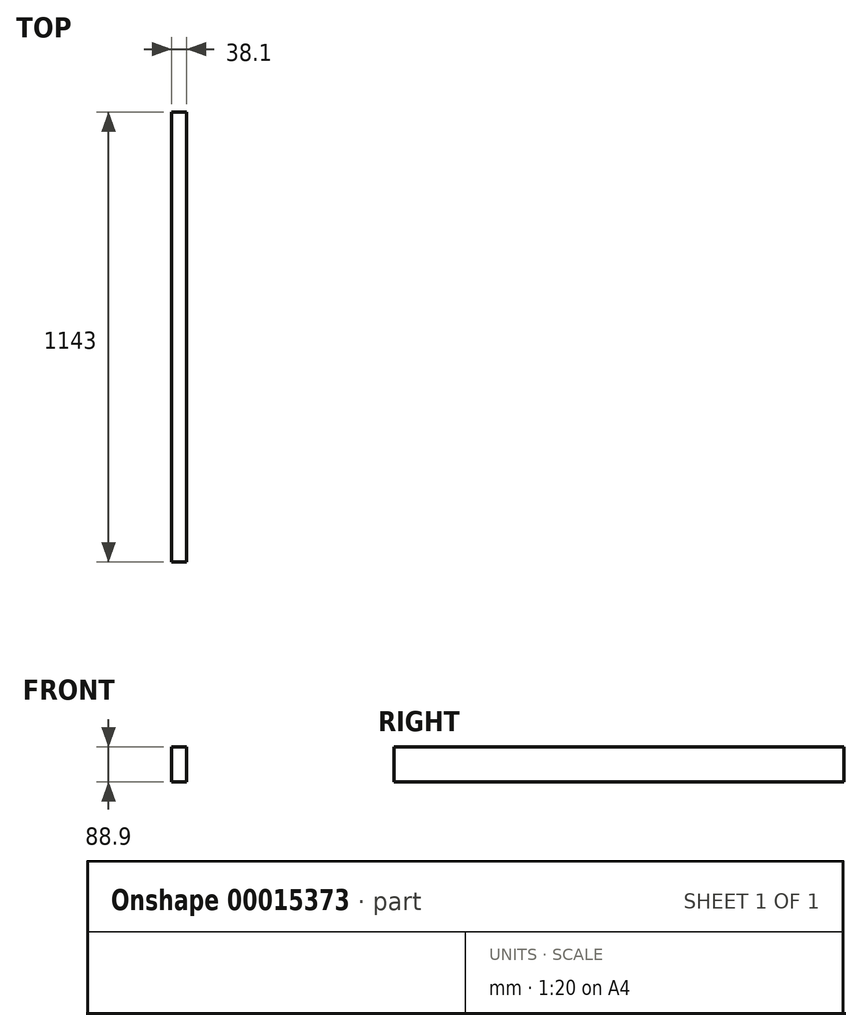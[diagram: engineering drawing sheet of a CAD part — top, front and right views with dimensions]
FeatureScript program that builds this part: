
annotation { "Feature Type Name" : "Feature", "Feature Type Description" : "" }
export const myFeature = defineFeature(function(context is Context, id is Id, definition is map)
    precondition{}
    {
        {
            var Q0;
            Q0=qCreatedBy(makeId("Front.planeOp"),FACE);
            var sketch = newSketch(context, id + "F0", { "sketchPlane" : qUnion([Q0])});
            skLineSegment(sketch, "E0.bottom", {"start": v(0, 0) * mm, "end": v(38.1, 0) * mm});
            skLineSegment(sketch, "E0.top", {"start": v(0, 88.9) * mm, "end": v(38.1, 88.9) * mm});
            skLineSegment(sketch, "E0.left", {"start": v(0, 0) * mm, "end": v(0, 88.9) * mm});
            skLineSegment(sketch, "E0.right", {"start": v(38.1, 0) * mm, "end": v(38.1, 88.9) * mm});
            skSolve(sketch);
        }
        {
            var Q0;
            Q0=makeQuery(id+"F0.imprint","IMPRINT",FACE,{"disambiguationData":[TD([[makeQuery(id+"F0.imprint","IMPRINT",EDGE,{"derivedFrom":sQuery(id+"F0.wireOp",EDGE,"E0.bottom")}),1.0]])]});
            extrude(context, id + "F1", {"entities" : qUnion([Q0]), "depth" : 1143 * mm});
        }
    });
